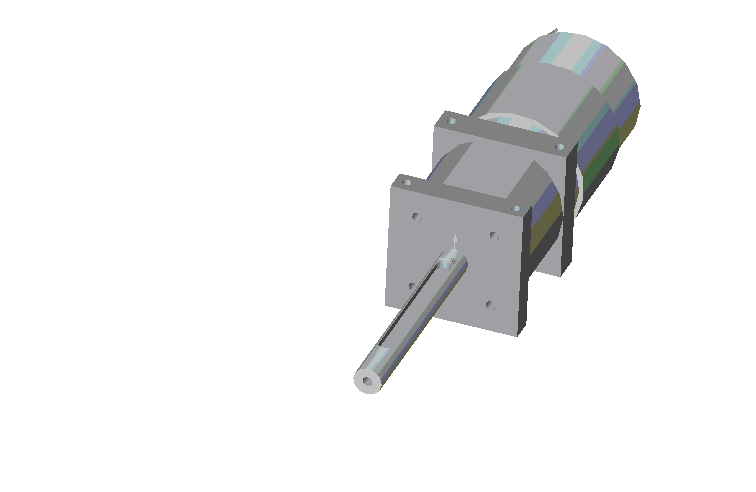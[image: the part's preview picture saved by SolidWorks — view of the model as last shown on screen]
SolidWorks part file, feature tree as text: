
SOLIDWORKS PART (.sldprt)
format: sldprt  version: not decoded by parser v0  size: 681,472 bytes
history: native  units: mm
features: sketch x13, extrude x8, cut_extrude x5, plane x2 (+8 scaffold rows collapsed)
feature tree (36):
  scaffold x8  (default folders/planes/origin — collapsed)
  sketch  "Sketch1"  dims[D1=13.97mm D2=13.97mm D3=27.94mm D4=27.94mm]
  extrude  "Base-Extrude"  Depth=5.08mm
  sketch  "Sketch2"  dims[D1=27.94mm]
  extrude  "Boss-Extrude1"  Depth=19.05mm
  sketch  "Sketch3"
  extrude  "Boss-Extrude2"  Depth=6.35mm
  sketch  "Sketch4"  dims[D1=26.924mm]
  extrude  "Boss-Extrude3"  Depth=38.1mm
  sketch  "Sketch5"  dims[D1=9.525mm]
  extrude  "Boss-Extrude4"  Depth=3.175mm
  sketch  "Sketch6"  dims[D1=6.0mm]
  extrude  "Boss-Extrude5"  Depth=48.26mm
  sketch  "Sketch7"  dims[D9=2.032mm D10=2.032mm D11=2.032mm D12=2.032mm D1=2.54mm D2=2.54mm D3=3.175mm D4=3.175mm D5=2.54mm D6=2.54mm D7=2.54mm D8=2.54mm]
  cut_extrude  "Cut-Extrude1"  [1 undecoded]
  sketch  "Sketch8"  dims[D1=2.032mm D2=5.842mm D3=22.098mm D4=5.842mm D5=22.098mm]
  cut_extrude  "Cut-Extrude2"  Depth=7.62mm
  sketch  "Sketch9"  dims[D1=2.032mm]
  cut_extrude  "Cut-Extrude3"  Depth=6.35mm
  plane  "Plane1"  Offset=1.27mm
  sketch  "Sketch10"  dims[c1.D3=1.5875mm c1.D2=1.5875mm c1.D1=3.175mm c2.D2=10.16mm c2.D3=31.75mm c2.D4=1.5875mm c3.D3=31.75mm c3.D2=10.16mm]
  cut_extrude  "Cut-Extrude4"  Depth=6.35mm
  sketch  "Sketch11"  dims[c1.D1=~1.411531mm c2.D1=90.0deg c3.D1=29.337mm c4.D1=45.0deg c4.D2=22.86mm c4.D3=0.381mm c4.D4=0.381mm c4.D5=11.43mm c4.D6=3.175mm c4.D7=3.175mm c4.D8=1.5875mm]
  extrude  "Boss-Extrude6"  Depth=6.35mm
  sketch  "Sketch12"  dims[D3=1.27mm D1=1.778mm D2=1.5875mm]
  cut_extrude  "Cut-Extrude5"  [1 undecoded]
  plane  "Plane3"  Offset=3.81mm
  sketch  "Sketch13"  dims[c1.D1=28.956mm c1.D2=26.924mm c1.D3=~21.203469mm c2.D3=45.0deg c2.D4=4.2164mm c2.D5=2.1082mm]
  extrude  "Boss-Extrude7"  Depth=20.066mm
decode coverage: 23 of 26 modeling features carry decoded parameters
note: ~ marks probable driven/reference dimensions
note: 2 parameter values undecoded
note: suppression state not decoded; provenance and decode notes live in map.json
